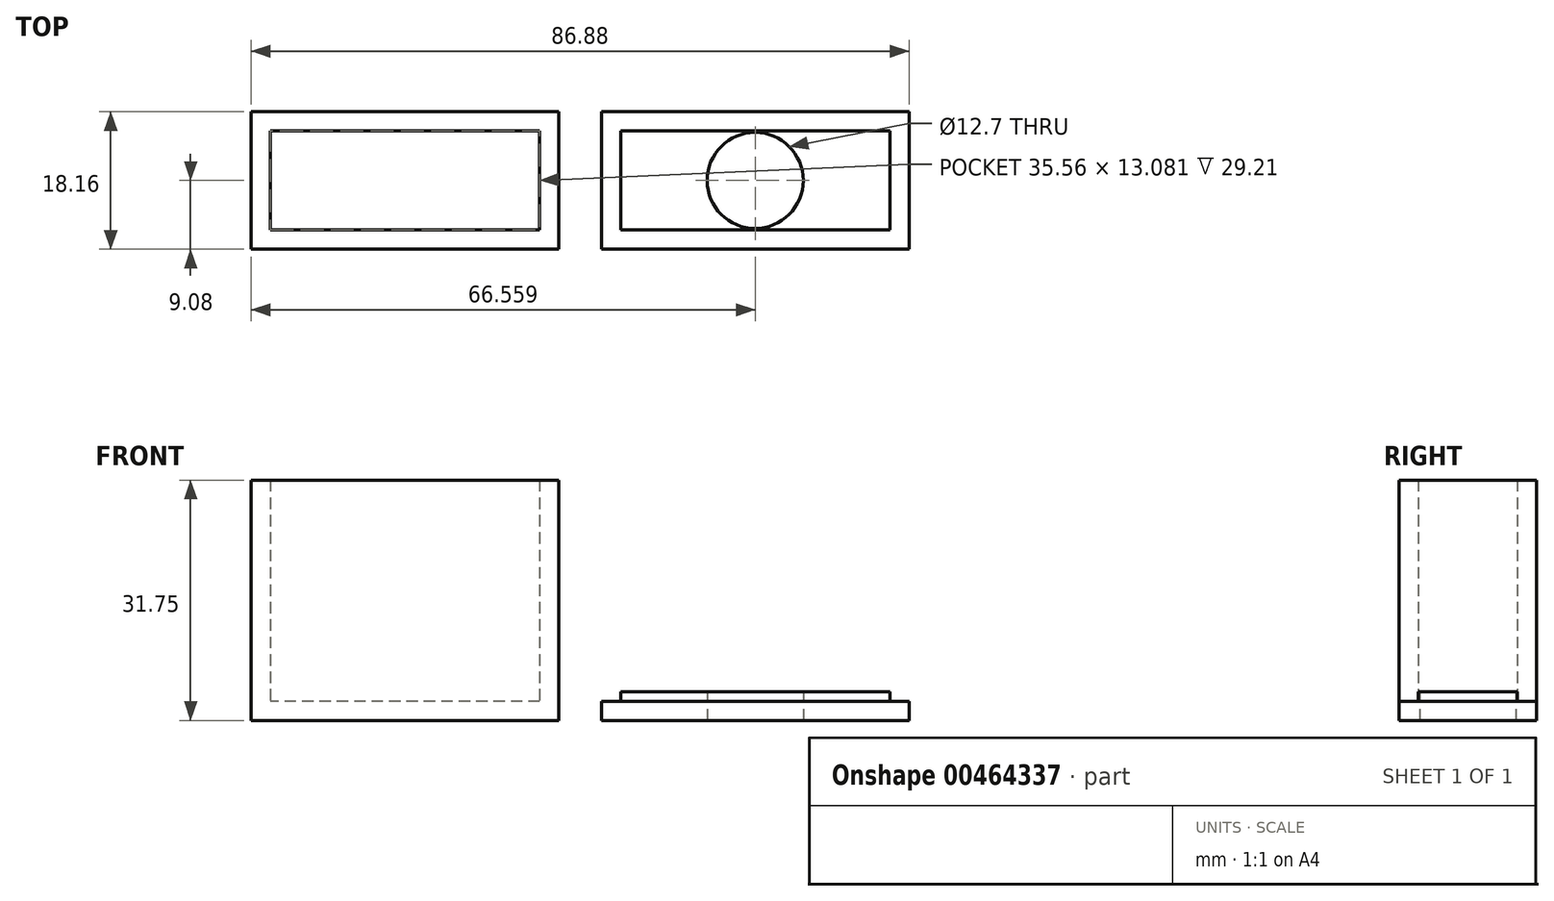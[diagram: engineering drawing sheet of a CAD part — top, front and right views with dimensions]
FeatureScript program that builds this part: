
annotation { "Feature Type Name" : "Feature", "Feature Type Description" : "" }
export const myFeature = defineFeature(function(context is Context, id is Id, definition is map)
    precondition{}
    {
        {
            var Q0;
            Q0=qCreatedBy(makeId("Top.planeOp"),FACE);
            var sketch = newSketch(context, id + "F0", { "sketchPlane" : qUnion([Q0])});
            skLineSegment(sketch, "E0.bottom", {"start": v(20.32, 9.08) * mm, "end": v(-20.32, 9.08) * mm});
            skLineSegment(sketch, "E0.top", {"start": v(20.32, -9.08) * mm, "end": v(-20.32, -9.08) * mm});
            skLineSegment(sketch, "E0.left", {"start": v(20.32, 9.08) * mm, "end": v(20.32, -9.08) * mm});
            skLineSegment(sketch, "E0.right", {"start": v(-20.32, 9.08) * mm, "end": v(-20.32, -9.08) * mm});
            skPoint(sketch, "E0.middle", {"position": v(0, 0) * mm});
            skSolve(sketch);
        }
        {
            var Q0;
            Q0=makeQuery(id+"F0.imprint","IMPRINT",FACE,{"disambiguationData":[TD([[makeQuery(id+"F0.imprint","IMPRINT",EDGE,{"derivedFrom":sQuery(id+"F0.wireOp",EDGE,"E0.bottom")}),1.0]])]});
            extrude(context, id + "F1", {"entities" : qUnion([Q0]), "depth" : 31.75 * mm});
        }
        {
            var Q0;
            Q0=makeQuery(id+"F1.opExtrude","CAP_FACE",FACE,{"disambiguationData":[OSD([sQuery(id+"F0.wireOp",EDGE,"E0.bottom"),sQuery(id+"F0.wireOp",EDGE,"E0.top"),sQuery(id+"F0.wireOp",EDGE,"E0.left"),sQuery(id+"F0.wireOp",EDGE,"E0.right")])],"isStart":false});
            shell(context, id + "F2", {"entities" : qUnion([Q0]), "thickness" : 2.54 * mm});
        }
        {
            var Q0;
            Q0=qCreatedBy(makeId("Top.planeOp"),FACE);
            var sketch = newSketch(context, id + "F3", { "sketchPlane" : qUnion([Q0])});
            skLineSegment(sketch, "E1.bottom", {"start": v(25.92, -9.08) * mm, "end": v(66.56, -9.08) * mm});
            skLineSegment(sketch, "E1.top", {"start": v(25.92, 9.08) * mm, "end": v(66.56, 9.08) * mm});
            skLineSegment(sketch, "E1.left", {"start": v(25.92, -9.08) * mm, "end": v(25.92, 9.08) * mm});
            skLineSegment(sketch, "E1.right", {"start": v(66.56, -9.08) * mm, "end": v(66.56, 9.08) * mm});
            skPoint(sketch, "E1.middle", {"position": v(46.24, 0) * mm});
            skLineSegment(sketch, "E2.bottom", {"start": v(64.02, 6.54) * mm, "end": v(28.46, 6.54) * mm});
            skLineSegment(sketch, "E2.top", {"start": v(64.02, -6.54) * mm, "end": v(28.46, -6.54) * mm});
            skLineSegment(sketch, "E2.left", {"start": v(64.02, 6.54) * mm, "end": v(64.02, -6.54) * mm});
            skLineSegment(sketch, "E2.right", {"start": v(28.46, 6.54) * mm, "end": v(28.46, -6.54) * mm});
            skCircle(sketch, "E3", {"center": v(46.24, 0) * mm, "radius": 6.35 * mm});
            skSolve(sketch);
        }
        {
            var Q0;
            Q0=makeQuery(id+"F3.imprint","IMPRINT",FACE,{"disambiguationData":[TD([[makeQuery(id+"F3.imprint","IMPRINT",EDGE,{"derivedFrom":sQuery(id+"F3.wireOp",EDGE,"E1.bottom")}),1.0]])]});
            var Q1;
            Q1=sQuery(id+"F3.wireOp",EDGE,"E1.bottom");
            var Q2;
            Q2=sQuery(id+"F3.wireOp",EDGE,"E1.left");
            var Q3;
            Q3=sQuery(id+"F3.wireOp",EDGE,"E1.top");
            var Q4;
            Q4=sQuery(id+"F3.wireOp",EDGE,"E1.right");
            var Q5;
            Q5=sQuery(id+"F3.wireOp",EDGE,"E2.top");
            var Q6;
            Q6=sQuery(id+"F3.wireOp",EDGE,"E2.bottom");
            var Q7;
            Q7=sQuery(id+"F3.wireOp",EDGE,"E2.left");
            extrude(context, id + "F4", {"entities" : qUnion([Q0]), "surfaceEntities" : qUnion([Q1, Q2, Q3, Q4, Q5, Q6, Q7]), "depth" : 2.54 * mm});
        }
        {
            var Q0;
            Q0=makeQuery(id+"F3.imprint","IMPRINT",FACE,{"disambiguationData":[TD([[makeQuery(id+"F3.imprint","IMPRINT",EDGE,{"derivedFrom":sQuery(id+"F3.wireOp",EDGE,"E2.bottom")}),1.0]])]});
            extrude(context, id + "F5", {"entities" : qUnion([Q0]), "operationType" : NewBodyOperationType.ADD, "depth" : 3.8 * mm});
        }
    });
